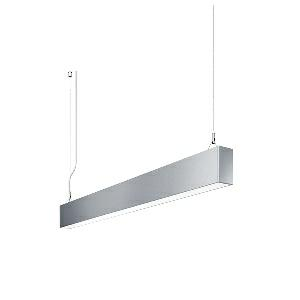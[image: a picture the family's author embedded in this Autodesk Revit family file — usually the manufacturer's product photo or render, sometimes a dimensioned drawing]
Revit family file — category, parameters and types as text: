
# Revit family: idoo_line_-_ilp_3000_830_d_00805725_b58a
name_source: partatom
category: Lighting Fixtures
units: mm (PartAtom-declared; Revit-internal decimal feet)

## family parameters
Cut with Voids When Loaded = No
Host = Face
Light Source = No
Part Type = Normal
Room Calculation Point = No
Round Connector Dimension = Use Diameter
Shared = No

## types (1)
- IDOO.line - ILP 3000/830/D (1 x LED, 3000 lm, 3000K)
    Apparent Load = 23 VA
    Approval mark = CE
    CIE Flux Codes = 66 91 98 40 100
    Color Rendering = 80-89
    Color Temperature = 3000K
    Control Gear = Electronic ballast
    Default Elevation = 1800 mm
    Description = ILP 3000/830/D|Suspended luminaire|light source: LED|connected load: 220-240V, 50/60Hz|Power consumption: approx. 23 W|standby: approx. 0,20|luminous flux: 3000 lm|luminous efficacy: 130 lm/W|light distribution: Direct/indirect|direct ratio: approx. 40 %|colour temperature: Warm white, ca. 3000 K|color rendering index (CRI): >= 80|chromaticity tolerance:  3 SDCM|System of protection: IP 40|technology: Continuously dimmable|luminaire body|material: Sectional aluminium|colour: Silver|lamp cover: Acrylic (PMMA), Clear|mains lead: 2.00 m With free stranded wires|Fastening: Steel cable 0.3 - 0.7 m|glare control: Prism aperture|luminance(L65): <= 2700 cd/m|unified glare rating(4H 8H): <=  16|special features: DALI Load 1x, TouchDIM - dimming via standard switch, Flicker-free, Suitable as emergency lighting|
    Frequency = 50 Hz
    Height = 110 mm
    Lamp = 1 x LED
    Lamp Light Flux = 3000 lm
    Lamp count = 1
    Length = 1134 mm
    Luminous efficacy = 130 lm/W
    Manufacturer = Waldmann
    ModVariant = No
    Model = 00805725
    Mounting Place = Ceiling
    Mounting Type = Pendant
    Number of Poles = 1
    OnlyDefault = Yes
    Power Factor = 1
    Product Name = IDOO.line - ILP 3000/830/D
    Product group = Suspended luminaire
    ProductGroupID = 9
    Protection Class = Protection class I
    Protection Degree = IP 40
    RLX_Detail_Level = 1
    RLX_Emergency_Light_Flux = 0 lm
    RLX_Emergency_Type = 0
    RLX_Emergency_Type_DB = No
    RlxData = <blob elided: 20821 chars, md5=b1a91bac>
    Socket = socket
    Standby Power = 0 W
    System Light Flux = 3000 lm
    System Power = 23 W
    Type Comments = Product without accessories
    Type Image = 113290000-00692519.jpg
    URL = http://relux.com
    VarID = ---
    Voltage = 230 V
    Voltage Range = 220-240 V
    Weight = 0.00 kg
    Width = 60 mm  [stored 0.19685 ft]

note: [stored X ft] marks values corroborated as IEEE doubles in the binary element streams (Revit-internal decimal feet)

## geometry (parser evidence)
native form markers: Blend x4, Sweep x14
no freeform markers — native parametric forms only
